# Revit family: Building-IEC309Connections-GEWISS-67IB-INTERLOCKED-SOCKET-OUTLETS_IP67_WITH_BOTTOM
name_source: partatom
category: Apparecchi elettrici
units: mm (PartAtom-declared; Revit-internal decimal feet)

## family parameters
Condiviso = Sì
Host = Superficie
Mantenere orientamento annotazione = Sì
Punto di calcolo locali = Sì
Quota connettore circolare = Usa diametro
Taglio con vuoti quando caricato = Sì
Tipo di parte = Normale

## types (23) — shared parameters
Catalogue = BUILDING
Catalogue Range = 67 IB
Corpo presa = GEWISS -BLU
Electrocod = 2222
Frequency = 50/60 Hz
Glow Wire Test = 850 °C (IB socket) - 650 °C (bottom)
Glow wire test: = 850 °C (IB socket) - 650 °C (bottom)
IDF = c396004b-a83b-4ac0-a4fa-669de3df814d
IDT = 80fd8aa3-f4ad-4bf9-871a-178f60767a59
IP degree = IP67
Immagine tipo = E.jpg
Operating temperature: = -25 +40 °C
Produttore = GEWISS S.p.A.
Prospetto di default = 1219 mm
Protection = NO (SBF)
Rated frequency (Hz) = 50/60 Hz
SEO = Socket outlet
Shock resistance = IK08
Simbolo presa = PRESAINDSTAGNA : 3P
Struttura = Grigio RAL - 7035
Technical sheet = https://www.gewiss.com
Thermo-pressure with ball = 125 °C (IB socket) - 80 °C (bottom)
Typology = Vertical
URL = https://www.gewiss.com
Version file RFA = 21.4
With back-mounting box = Yes
Working temperature = -25 ÷ +40 °C
presa = Giallo
zero-valued in all types: giallo

## per-type parameters (varying)
| type | Colour | Colour: | Descrizione | EAN code | Modello | No. of poles | Number of poles | Rated current (A) | Rated current (In) | Rated voltage | Rated voltage: | Reference h |
| GW66217N - 32A 3P+N+E 230V V.INT.SOCK.O.W.B.9H SBF | Blue | Blue | 32A 3P+N+E 230V V.INT.SOCK.O.W.B.9H SBF | 8011564741287 | GW66217N | 3P+N+E | 3P+N+E | 32 | 32 | 200 - 250 V | 200 - 250 V | 9 |
| GW66218N - 32A 2P+E 400V V.INT.SOCK.O.W.B.9H SBF | Red | Red | 32A 2P+E 400V V.INT.SOCK.O.W.B.9H SBF | 8011564741294 | GW66218N | 2P+E | 2P+E | 32 | 32 | 380 - 415 V | 380 - 415 V | 9 |
| GW66220N - 32A 3P+N+E 400V V.INT.SOCK.O.W.B.6H SBF | Red | Red | 32A 3P+N+E 400V V.INT.SOCK.O.W.B.6H SBF | 8011564742536 | GW66220N | 3P+N+E | 3P+N+E | 32 | 32 | 380 - 415 V | 380 - 415 V | 6 |
| GW66211N - 16A 3P+N+E 500V V.INT.SOCK.O.W.B.7H SBF | Black | Black | 16A 3P+N+E 500V V.INT.SOCK.O.W.B.7H SBF | 8011564741232 | GW66211N | 3P+N+E | 3P+N+E | 16 | 16 | 480 - 500 V | 480 - 500 V | 7 |
| GW66208N - 16A 3P+E 400V V.INT.SOCK.O.W.B.6H SBF | Red | Red | 16A 3P+E 400V V.INT.SOCK.O.W.B.6H SBF | 8011564741218 | GW66208N | 3P+E | 3P+E | 16 | 16 | 380 - 415 V | 380 - 415 V | 6 |
| GW66201N - 16A 2P+E 110V V.INT.SOCK.O.W.B.4H SBF | Yellow | Yellow | 16A 2P+E 110V V.INT.SOCK.O.W.B.4H SBF | 8011564741140 | GW66201N | 2P+E | 2P+E | 16 | 16 | 100 - 130 V | 100 - 130 V | 4 |
| GW66204N - 16A 2P+E 230V V.INT.SOCK.O.W.B.6H SBF | Blue | Blue | 16A 2P+E 230V V.INT.SOCK.O.W.B.6H SBF | 8011564741171 | GW66204N | 2P+E | 2P+E | 16 | 16 | 200 - 250 V | 200 - 250 V | 6 |
| GW66216N - 32A 3P+E 230V V.INT.SOCK.O.W.B.9H SBF | Blue | Blue | 32A 3P+E 230V V.INT.SOCK.O.W.B.9H SBF | 8011564741270 | GW66216N | 3P+E | 3P+E | 32 | 32 | 200 - 250 V | 200 - 250 V | 9 |
| GW66207N - 16A 2P+E 400V V.INT.SOCK.O.W.B.9H SBF | Red | Red | 16A 2P+E 400V V.INT.SOCK.O.W.B.9H SBF | 8011564741201 | GW66207N | 2P+E | 2P+E | 16 | 16 | 380 - 415 V | 380 - 415 V | 9 |
| GW66209N - 16A 3P+N+E 400V V.INT.SOCK.O.W.B.6H SBF | Red | Red | 16A 3P+N+E 400V V.INT.SOCK.O.W.B.6H SBF | 8011564742512 | GW66209N | 3P+N+E | 3P+N+E | 16 | 16 | 380 - 415 V | 380 - 415 V | 6 |
| GW66214N - 32A 3P+N+E 110V V.INT.SOCK.O.W.B.4H SBF | Yellow | Yellow | 32A 3P+N+E 110V V.INT.SOCK.O.W.B.4H SBF | 8011564741263 | GW66214N | 3P+N+E | 3P+N+E | 32 | 32 | 100 - 130 V | 100 - 130 V | 4 |
| GW66221N - 32A 3P+E 500V V.INT.SOCK.O.W.B.7H SBF | Black | Black | 32A 3P+E 500V V.INT.SOCK.O.W.B.7H SBF | 8011564741317 | GW66221N | 3P+E | 3P+E | 32 | 32 | 480 - 500 V | 480 - 500 V | 7 |
| GW66212N - 32A 2P+E 110V V.INT.SOCK.O.W.B.4H SBF | Yellow | Yellow | 32A 2P+E 110V V.INT.SOCK.O.W.B.4H SBF | 8011564741249 | GW66212N | 2P+E | 2P+E | 32 | 32 | 100 - 130 V | 100 - 130 V | 4 |
| GW66257N - 32A 3P+E 380V V.INT.SOCK.O.W.B.3H SBF | Red | Red | 32A 3P+E 380V V.INT.SOCK.O.W.B.3H SBF | 8011564741522 | GW66257N | 3P+E | 3P+E | 32 | 32 | 380 - 440 V | 380 - 440 V | 3 |
| GW66219N - 32A 3P+E 400V V.INT.SOCK.O.W.B.6H SBF | Red | Red | 32A 3P+E 400V V.INT.SOCK.O.W.B.6H SBF | 8011564741300 | GW66219N | 3P+E | 3P+E | 32 | 32 | 380 - 415 V | 380 - 415 V | 6 |
| GW66210N - 16A 3P+E 500V V.INT.SOCK.O.W.B.7H SBF | Black | Black | 16A 3P+E 500V V.INT.SOCK.O.W.B.7H SBF | 8011564741225 | GW66210N | 3P+E | 3P+E | 16 | 16 | 480 - 500 V | 480 - 500 V | 7 |
| GW66202N - 16A 3P+E 110V V.INT.SOCK.O.W.B.4H SBF | Yellow | Yellow | 16A 3P+E 110V V.INT.SOCK.O.W.B.4H SBF | 8011564741157 | GW66202N | 3P+E | 3P+E | 16 | 16 | 100 - 130 V | 100 - 130 V | 4 |
| GW66215N - 32A 2P+E 230V V.INT.SOCK.O.W.B.6H SBF | Blue | Blue | 32A 2P+E 230V V.INT.SOCK.O.W.B.6H SBF | 8011564742529 | GW66215N | 2P+E | 2P+E | 32 | 32 | 200 - 250 V | 200 - 250 V | 6 |
| GW66206N - 16A 3P+N+E 230V V.INT.SOCK.O.W.B.9H SBF | Blue | Blue | 16A 3P+N+E 230V V.INT.SOCK.O.W.B.9H SBF | 8011564741195 | GW66206N | 3P+N+E | 3P+N+E | 16 | 16 | 200 - 250 V | 200 - 250 V | 9 |
| GW66222N - 32A 3P+N+E 500V V.INT.SOCK.O.W.B.7H SBF | Black | Black | 32A 3P+N+E 500V V.INT.SOCK.O.W.B.7H SBF | 8011564741324 | GW66222N | 3P+N+E | 3P+N+E | 32 | 32 | 480 - 500 V | 480 - 500 V | 7 |
| GW66203N - 16A 3P+N+E 110V V.INT.SOCK.O.W.B.4H SBF | Yellow | Yellow | 16A 3P+N+E 110V V.INT.SOCK.O.W.B.4H SBF | 8011564741164 | GW66203N | 3P+N+E | 3P+N+E | 16 | 16 | 100 - 130 V | 100 - 130 V | 4 |
| GW66213N - 32A 3P+E 110V V.INT.SOCK.O.W.B.4H SBF | Yellow | Yellow | 32A 3P+E 110V V.INT.SOCK.O.W.B.4H SBF | 8011564741256 | GW66213N | 3P+E | 3P+E | 32 | 32 | 100 - 130 V | 100 - 130 V | 4 |
| GW66205N - 16A 3P+E 230V V.INT.SOCK.O.W.B.9H SBF | Blue | Blue | 16A 3P+E 230V V.INT.SOCK.O.W.B.9H SBF | 8011564741188 | GW66205N | 3P+E | 3P+E | 16 | 16 | 200 - 250 V | 200 - 250 V | 9 |

## geometry (parser evidence)
native form markers: Sweep x5
no freeform markers — native parametric forms only
